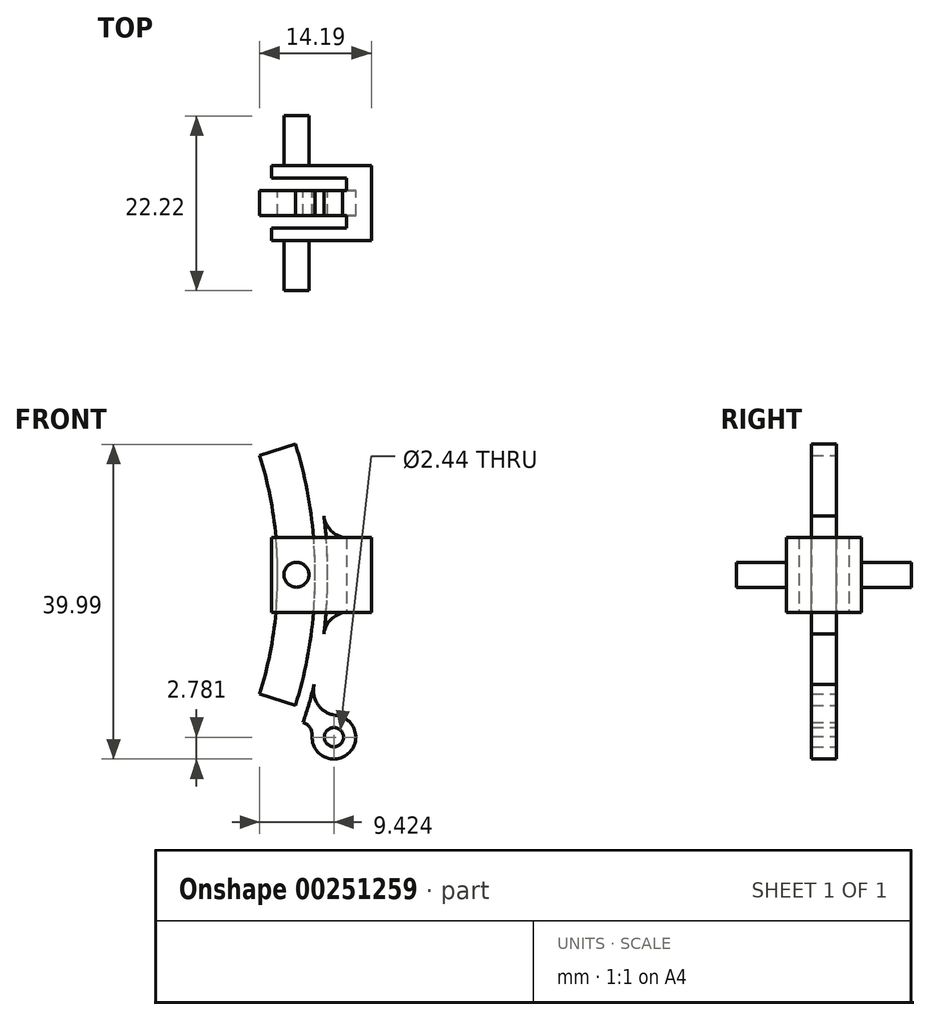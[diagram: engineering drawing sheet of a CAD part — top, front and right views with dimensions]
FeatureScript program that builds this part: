
annotation { "Feature Type Name" : "Feature", "Feature Type Description" : "" }
export const myFeature = defineFeature(function(context is Context, id is Id, definition is map)
    precondition{}
    {
        {
            var Q0;
            Q0=qCreatedBy(makeId("Front.planeOp"),FACE);
            var sketch = newSketch(context, id + "F0", { "sketchPlane" : qUnion([Q0])});
            skLineSegment(sketch, "E0.bottom", {"start": v(15.77, 52.02) * mm, "end": v(41.17, 52.02) * mm});
            skLineSegment(sketch, "E0.top", {"start": v(15.77, 7.57) * mm, "end": v(41.17, 7.57) * mm});
            skLineSegment(sketch, "E0.left", {"start": v(15.77, 52.02) * mm, "end": v(15.77, 7.57) * mm});
            skLineSegment(sketch, "E0.right", {"start": v(41.17, 52.02) * mm, "end": v(41.17, 7.57) * mm});
            skLineSegment(sketch, "E1", {"start": v(-27.75, 29.8) * mm, "end": v(53.68, 29.8) * mm, "construction": true});
            skLineSegment(sketch, "E2", {"start": v(2.64, 45.67) * mm, "end": v(53.6, 45.67) * mm, "construction": true});
            skLineSegment(sketch, "E3", {"start": v(26.22, 60.99) * mm, "end": v(26.22, 3.12) * mm, "construction": true});
            skLineSegment(sketch, "E4", {"start": v(3.94, 13.92) * mm, "end": v(54.54, 13.92) * mm, "construction": true});
            skArc(sketch, "E5", {"start": v(23.32, 12.34) * mm, "mid": v(26.22, 29.8) * mm, "end": v(23.32, 47.26) * mm, "construction": true});
            skLineSegment(sketch, "E6", {"start": v(-27.75, 29.8) * mm, "end": v(41.17, 51) * mm, "construction": true});
            skLineSegment(sketch, "E7", {"start": v(-27.75, 29.8) * mm, "end": v(41.17, 8.59) * mm, "construction": true});
            skArc(sketch, "E8", {"start": v(21.56, 44.97) * mm, "mid": v(23.84, 29.8) * mm, "end": v(21.56, 14.62) * mm});
            skArc(sketch, "E9", {"start": v(26.1, 46.37) * mm, "mid": v(28.6, 29.8) * mm, "end": v(26.1, 13.22) * mm});
            skLineSegment(sketch, "E10", {"start": v(2.1, 47.26) * mm, "end": v(50.43, 47.26) * mm, "construction": true});
            skLineSegment(sketch, "E11", {"start": v(3.95, 12.34) * mm, "end": v(47.89, 12.34) * mm, "construction": true});
            skLineSegment(sketch, "E12", {"start": v(-27.75, 29.8) * mm, "end": v(37.25, 52.02) * mm, "construction": true});
            skLineSegment(sketch, "E13", {"start": v(-27.75, 29.8) * mm, "end": v(37.25, 7.57) * mm, "construction": true});
            skArc(sketch, "E14", {"start": v(19.56, 45.98) * mm, "mid": v(22.25, 29.8) * mm, "end": v(19.56, 13.62) * mm});
            skArc(sketch, "E15", {"start": v(27.07, 48.55) * mm, "mid": v(30.2, 29.8) * mm, "end": v(27.07, 11.05) * mm});
            skLineSegment(sketch, "E16", {"start": v(21.56, 44.97) * mm, "end": v(26.1, 46.37) * mm});
            skLineSegment(sketch, "E17", {"start": v(19.56, 45.98) * mm, "end": v(27.07, 48.55) * mm});
            skLineSegment(sketch, "E18", {"start": v(21.56, 14.62) * mm, "end": v(26.1, 13.22) * mm});
            skLineSegment(sketch, "E19", {"start": v(19.56, 13.62) * mm, "end": v(27.07, 11.05) * mm});
            skLineSegment(sketch, "E20", {"start": v(30.98, 59.22) * mm, "end": v(30.98, -1.54) * mm, "construction": true});
            skCircle(sketch, "E21", {"center": v(30.98, 9.16) * mm, "radius": 1.22 * mm});
            skCircle(sketch, "E22", {"center": v(30.98, 9.16) * mm, "radius": 2.78 * mm});
            skLineSegment(sketch, "E23", {"start": v(26.22, 63.33) * mm, "end": v(26.22, -3.89) * mm, "construction": true});
            skArc(sketch, "E24", {"start": v(27.07, 11.05) * mm, "mid": v(27.95, 10.36) * mm, "end": v(28.2, 9.27) * mm});
            skArc(sketch, "E25", {"start": v(28.49, 15.85) * mm, "mid": v(28.97, 13.25) * mm, "end": v(31.26, 11.93) * mm});
            skLineSegment(sketch, "E26", {"start": v(30, 34.56) * mm, "end": v(34.16, 34.56) * mm});
            skLineSegment(sketch, "E27", {"start": v(34.16, 34.56) * mm, "end": v(34.16, 25.04) * mm});
            skLineSegment(sketch, "E28", {"start": v(34.16, 25.04) * mm, "end": v(30, 25.04) * mm});
            skArc(sketch, "E29", {"start": v(29.71, 37.23) * mm, "mid": v(30.48, 35.53) * mm, "end": v(32.08, 34.56) * mm});
            skArc(sketch, "E30", {"start": v(32.85, 25.04) * mm, "mid": v(30.75, 24.25) * mm, "end": v(29.7, 22.27) * mm});
            skSolve(sketch);
        }
        {
            var Q0;
            {var subQ0=sQuery(id+"F0.wireOp",EDGE,"E22");var subQ1=sQuery(id+"F0.wireOp",EDGE,"E0.top");var subQ2=makeQuery(id+"F0.imprint","INTERSECT",VERTEX,{"disambiguationData":[OD(0.0)],"derivedFrom":[subQ1,subQ0]});Q0=makeQuery(id+"F0.imprint","IMPRINT",FACE,{"disambiguationData":[TD([[makeQuery(id+"F0.imprint","IMPRINT",EDGE,{"disambiguationData":[TD([[subQ2,-1.0]])],"derivedFrom":subQ1}),-1.0]])]});}
            var Q1;
            Q1=makeQuery(id+"F0.imprint","IMPRINT",FACE,{"disambiguationData":[TD([[makeQuery(id+"F0.imprint","IMPRINT",EDGE,{"derivedFrom":sQuery(id+"F0.wireOp",EDGE,"E21")}),-1.0]])]});
            var Q2;
            Q2=makeQuery(id+"F0.imprint","IMPRINT",FACE,{"disambiguationData":[TD([[makeQuery(id+"F0.imprint","IMPRINT",EDGE,{"derivedFrom":sQuery(id+"F0.wireOp",EDGE,"E8")}),-1.0]])]});
            var Q3;
            {var subQ0=sQuery(id+"F0.wireOp",EDGE,"E27");Q3=makeQuery(id+"F0.imprint","IMPRINT",FACE,{"disambiguationData":[TD([[makeQuery(id+"F0.imprint","IMPRINT",EDGE,{"derivedFrom":subQ0}),-1.0]])]});}
            var Q4;
            {var subQ3=sQuery(id+"F0.wireOp",EDGE,"E29");Q4=makeQuery(id+"F0.imprint","IMPRINT",FACE,{"disambiguationData":[TD([[makeQuery(id+"F0.imprint","IMPRINT",EDGE,{"derivedFrom":subQ3}),-1.0]])]});}
            var Q5;
            {var subQ3=sQuery(id+"F0.wireOp",EDGE,"E30");Q5=makeQuery(id+"F0.imprint","IMPRINT",FACE,{"disambiguationData":[TD([[makeQuery(id+"F0.imprint","IMPRINT",EDGE,{"derivedFrom":subQ3}),-1.0]])]});}
            var Q6;
            {var subQ3=sQuery(id+"F0.wireOp",EDGE,"E25");Q6=makeQuery(id+"F0.imprint","IMPRINT",FACE,{"disambiguationData":[TD([[makeQuery(id+"F0.imprint","IMPRINT",EDGE,{"derivedFrom":subQ3}),-1.0]])]});}
            extrude(context, id + "F1", {"entities" : qUnion([Q0, Q1, Q2, Q3, Q4, Q5, Q6]), "depth" : 3.17 * mm});
        }
        {
            var Q0;
            Q0=makeQuery(id+"F1.opExtrude","SWEPT_FACE",FACE,{"disambiguationData":[OSD([sQuery(id+"F0.wireOp",EDGE,"E27")])]});
            var sketch = newSketch(context, id + "F2", { "sketchPlane" : qUnion([Q0])});
            skLineSegment(sketch, "E31", {"start": v(-6.35, 34.56) * mm, "end": v(3.18, 34.56) * mm});
            skLineSegment(sketch, "E32", {"start": v(3.18, 34.56) * mm, "end": v(3.18, 25.04) * mm});
            skLineSegment(sketch, "E33", {"start": v(3.18, 25.04) * mm, "end": v(-6.35, 25.04) * mm});
            skLineSegment(sketch, "E34", {"start": v(-6.35, 25.04) * mm, "end": v(-6.35, 34.56) * mm});
            skSolve(sketch);
        }
        {
            var Q0;
            Q0 = qSketchRegion(id + "F2", true);
            extrude(context, id + "F3", {"entities" : qUnion([Q0]), "operationType" : NewBodyOperationType.ADD, "depth" : 1.59 * mm});
        }
        {
            var Q0;
            {var subQ0=sQuery(id+"F2.wireOp",EDGE,"E31");var subQ3=sQuery(id+"F2.wireOp",EDGE,"E33");var subQ4=sQuery(id+"F2.wireOp",EDGE,"E34");Q0=makeQuery(id+"F3.boolean.opBoolean","SPLIT",FACE,{"disambiguationData":[TD([makeQuery(id+"F3.opExtrude","SWEPT_FACE",FACE,{"disambiguationData":[OSD([subQ4])]})])],"derivedFrom":makeQuery(id+"F3.opExtrude","CAP_FACE",FACE,{"disambiguationData":[OSD([subQ0,sQuery(id+"F2.wireOp",EDGE,"E32"),subQ3,subQ4])],"isStart":true})});}
            var sketch = newSketch(context, id + "F4", { "sketchPlane" : qUnion([Q0])});
            skLineSegment(sketch, "E35.bottom", {"start": v(3.18, 34.56) * mm, "end": v(6.35, 34.56) * mm});
            skLineSegment(sketch, "E35.top", {"start": v(3.18, 25.04) * mm, "end": v(6.35, 25.04) * mm});
            skLineSegment(sketch, "E35.left", {"start": v(3.18, 34.56) * mm, "end": v(3.18, 25.04) * mm});
            skLineSegment(sketch, "E35.right", {"start": v(6.35, 34.56) * mm, "end": v(6.35, 25.04) * mm});
            skLineSegment(sketch, "E36.bottom", {"start": v(0, 34.56) * mm, "end": v(-3.17, 34.56) * mm});
            skLineSegment(sketch, "E36.top", {"start": v(0, 25.04) * mm, "end": v(-3.17, 25.04) * mm});
            skLineSegment(sketch, "E36.left", {"start": v(0, 34.56) * mm, "end": v(0, 25.04) * mm});
            skLineSegment(sketch, "E36.right", {"start": v(-3.17, 34.56) * mm, "end": v(-3.17, 25.04) * mm});
            skSolve(sketch);
        }
        {
            var Q0;
            Q0 = qSketchRegion(id + "F4", true);
            extrude(context, id + "F5", {"entities" : qUnion([Q0]), "operationType" : NewBodyOperationType.ADD, "depth" : 1.59 * mm});
        }
        {
            var Q0;
            Q0=makeQuery(id+"F5.opExtrude","CAP_FACE",FACE,{"disambiguationData":[OSD([sQuery(id+"F4.wireOp",EDGE,"E35.bottom"),sQuery(id+"F4.wireOp",EDGE,"E35.top"),sQuery(id+"F4.wireOp",EDGE,"E35.left"),sQuery(id+"F4.wireOp",EDGE,"E35.right")])],"isStart":false});
            var sketch = newSketch(context, id + "F6", { "sketchPlane" : qUnion([Q0])});
            skLineSegment(sketch, "E37", {"start": v(4.76, 34.56) * mm, "end": v(4.76, 25.04) * mm});
            skLineSegment(sketch, "E38", {"start": v(-1.59, 34.56) * mm, "end": v(-1.59, 25.04) * mm});
            skLineSegment(sketch, "E39.0", {"start": v(0, 34.56) * mm, "end": v(-3.17, 34.56) * mm});
            skLineSegment(sketch, "E40.0.0", {"start": v(-3.17, 25.04) * mm, "end": v(0, 25.04) * mm});
            skLineSegment(sketch, "E40.0.1", {"start": v(0, 25.04) * mm, "end": v(0, 34.56) * mm});
            skLineSegment(sketch, "E40.0.3", {"start": v(-3.17, 34.56) * mm, "end": v(-3.17, 25.04) * mm});
            skLineSegment(sketch, "E41.0.0", {"start": v(6.35, 25.04) * mm, "end": v(6.35, 34.56) * mm});
            skLineSegment(sketch, "E41.0.1", {"start": v(6.35, 34.56) * mm, "end": v(3.18, 34.56) * mm});
            skLineSegment(sketch, "E41.0.2", {"start": v(3.18, 34.56) * mm, "end": v(3.18, 25.04) * mm});
            skLineSegment(sketch, "E41.0.3", {"start": v(3.18, 25.04) * mm, "end": v(6.35, 25.04) * mm});
            skSolve(sketch);
        }
        {
            var Q0;
            {var subQ0=sQuery(id+"F6.wireOp",EDGE,"E38");Q0=makeQuery(id+"F6.imprint","IMPRINT",FACE,{"disambiguationData":[TD([[makeQuery(id+"F6.imprint","IMPRINT",EDGE,{"derivedFrom":subQ0}),-1.0]])]});}
            var Q1;
            {var subQ0=sQuery(id+"F6.wireOp",EDGE,"E37");Q1=makeQuery(id+"F6.imprint","IMPRINT",FACE,{"disambiguationData":[TD([[makeQuery(id+"F6.imprint","IMPRINT",EDGE,{"derivedFrom":subQ0}),1.0]])]});}
            extrude(context, id + "F7", {"entities" : qUnion([Q0, Q1]), "operationType" : NewBodyOperationType.ADD, "depth" : 9.52 * mm});
        }
        {
            var Q0;
            Q0=makeQuery(id+"F7.boolean.opBoolean","MERGE",FACE,{"derivedFrom":[makeQuery(id+"F5.boolean.opBoolean","MERGE",FACE,{"derivedFrom":[makeQuery(id+"F3.opExtrude","SWEPT_FACE",FACE,{"disambiguationData":[OSD([sQuery(id+"F2.wireOp",EDGE,"E34")])]}),makeQuery(id+"F5.opExtrude","SWEPT_FACE",FACE,{"disambiguationData":[OSD([sQuery(id+"F4.wireOp",EDGE,"E35.right")])]})]}),makeQuery(id+"F7.opExtrude","SWEPT_FACE",FACE,{"disambiguationData":[OSD([sQuery(id+"F6.wireOp",EDGE,"E41.0.0")])]})]});
            var sketch = newSketch(context, id + "F8", { "sketchPlane" : qUnion([Q0])});
            skCircle(sketch, "E42", {"center": v(26.22, 29.8) * mm, "radius": 1.59 * mm});
            skSolve(sketch);
        }
        {
            var Q0;
            Q0 = qSketchRegion(id + "F8", true);
            extrude(context, id + "F9", {"entities" : qUnion([Q0]), "operationType" : NewBodyOperationType.ADD, "depth" : 6.35 * mm});
        }
        {
            var Q0;
            Q0=makeQuery(id+"F7.boolean.opBoolean","MERGE",FACE,{"derivedFrom":[makeQuery(id+"F5.opExtrude","SWEPT_FACE",FACE,{"disambiguationData":[OSD([sQuery(id+"F4.wireOp",EDGE,"E36.right")])]}),makeQuery(id+"F7.opExtrude","SWEPT_FACE",FACE,{"disambiguationData":[OSD([sQuery(id+"F6.wireOp",EDGE,"E40.0.3")])]})]});
            var sketch = newSketch(context, id + "F10", { "sketchPlane" : qUnion([Q0])});
            skCircle(sketch, "E43", {"center": v(-26.22, 29.8) * mm, "radius": 1.59 * mm});
            skSolve(sketch);
        }
        {
            var Q0;
            Q0 = qSketchRegion(id + "F10", true);
            extrude(context, id + "F11", {"entities" : qUnion([Q0]), "operationType" : NewBodyOperationType.ADD, "depth" : 6.35 * mm});
        }
    });
